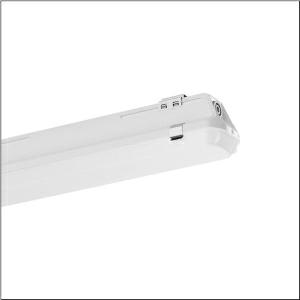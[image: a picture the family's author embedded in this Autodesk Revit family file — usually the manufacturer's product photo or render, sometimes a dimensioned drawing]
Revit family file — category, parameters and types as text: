
# Revit family: monsun_r__21_51fb12mp480b_d2d7
name_source: partatom
category: Lighting Fixtures
units: mm (PartAtom-declared; Revit-internal decimal feet)

## family parameters
Cut with Voids When Loaded = No
Host = Face
Light Source = No
Part Type = Normal
Room Calculation Point = No
Round Connector Dimension = Use Diameter
Shared = No

## types (1)
- --- (1 x LED, 8100 lm, 53.6 W, 4000K)
    Apparent Load = 54 VA
    CIE Flux Codes = 65 88 97 97 100
    Color Rendering = 80
    Color Temperature = 4000K
    Default Elevation = 1800 mm
    Description = Monsun® 21, damp-proof luminaire, chain hanger, primary light control with lens, primary optical cover: enclosure, of PMMA, light emission: direct distribution, primary light characteristic: symmetric, installation type: suspended mounting, surface-mounted, horizontal mounting, vertical mounting, LED, rated luminous flux: 8.100lm, luminous efficacy: 151lm/W, light colour: 840, colour temperature: 4000K, control gear: ECG, with terminal, 3-pole, max. 2.5mm², mains connection: 220..240V, AC, 50/60Hz, rated input power: 54W, housing, of glass-fibre reinforced polyester, uncoated, bright grey, incl. chain hanger, length: 1.590mm, width: 90mm, height: 88mm, clip for enclosure, of stainless steel (V2A), ceiling mounting element, of stainless steel (V2A), chain hanger, of stainless steel (V2A), protection rating (complete): IP66, insulation class (complete): insulation class I (protective earthing), certification: CE, ENEC, VDE, UKCA, protection symbol: D, impact resistance: IK04, permissible operating ambient temperature: -25..+35°C, standard: EN 50419, EN 60598-2-1, corresponds to IFS (International Featured Standards) requirements for safety and quality in the food industry, for indoor or canopied outdoor use, no direct snow, no direct sun, no direct rain, contact your sales advisor before using the luminaires in applications with unclear chemical exposure, large temperature fluctuations or condensation-forming humidity, LABS conformity tested according to VDMA 24364:2018-05, packaging unit: 1 piece
    Height = 89 mm
    Lamp = 1 x LED
    Lamp Light Flux = 8100 lm
    Lamp Power = 53.6 W
    Lamp count = 1
    Length = 1590 mm
    Luminous efficacy = 151 lm/W
    Manufacturer = Siteco
    ModVariant = No
    Model = 51FB12MP480B
    Mounting Place = Ceiling
    Mounting Type = Surface mounted
    Number of Poles = 1
    OnlyDefault = Yes
    Power Factor = 1
    Product Name = Monsun® 21
    Product group = damp-proof luminaire
    ProductGroupID = 300
    Protection Class = Protection class I
    Protection Degree = IP 66
    RLX_Detail_Level = 1
    RLX_Emergency_Light_Flux = 0 lm
    RLX_Emergency_Type = 0
    RLX_Emergency_Type_DB = No
    RlxData = <blob elided: 89741 chars, md5=d52b54ea>
    Socket = socket
    Standby Power = 0 W
    System Light Flux = 8100 lm
    System Power = 54 W
    Type Comments = factory setting: luminous flux: 100 % | (A | C | E) | 121 mA
    Type Image = l_1006717.jpg
    URL = http://relux.com
    VarID = @adj_079261
    Voltage = 0 V
    Weight = 0.00 kg
    Width = 90 mm

## geometry (parser evidence)
native form markers: Blend x4, Sweep x10
no freeform markers — native parametric forms only
